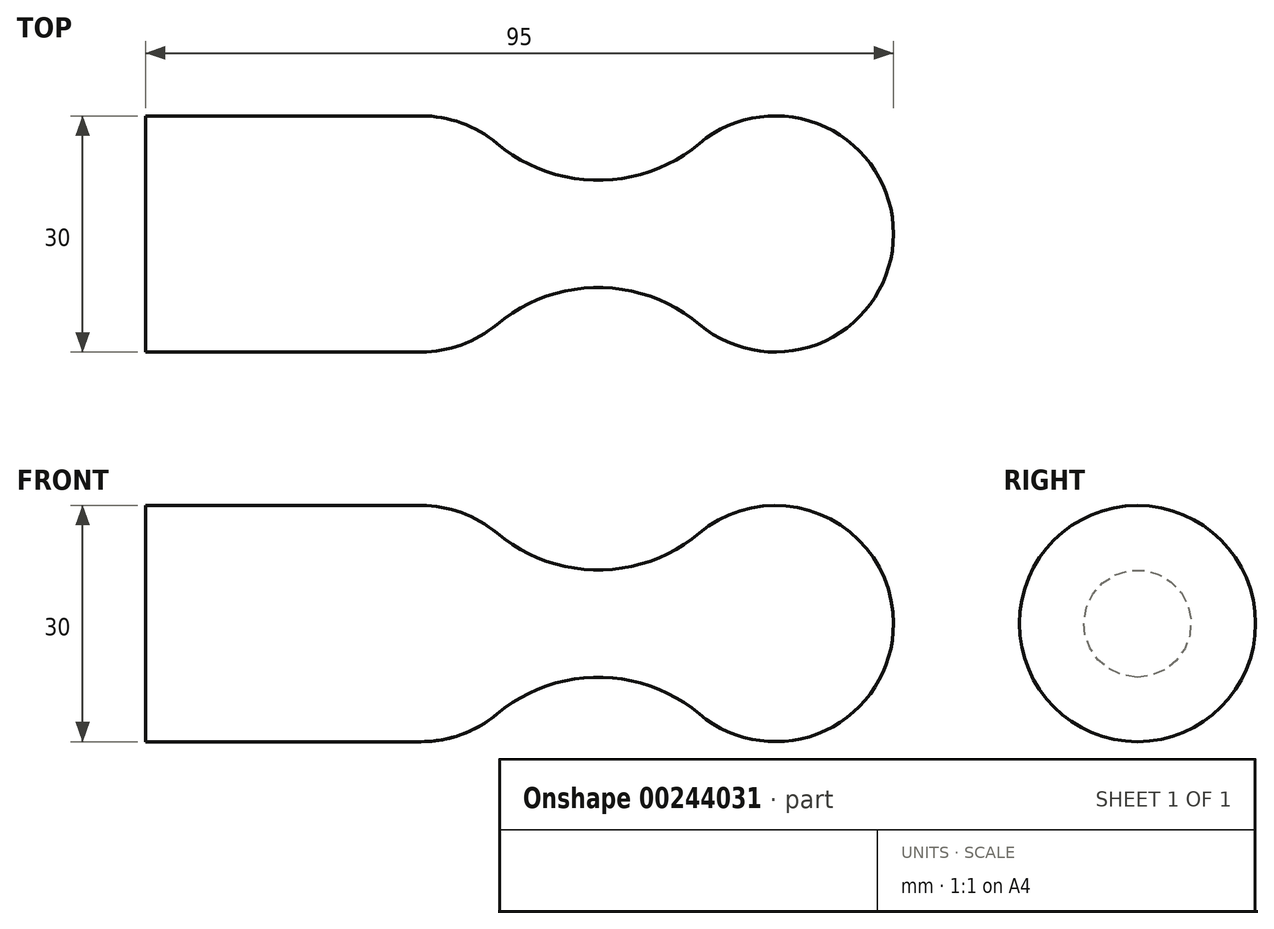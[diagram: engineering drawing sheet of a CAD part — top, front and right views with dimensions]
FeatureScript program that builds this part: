
annotation { "Feature Type Name" : "Feature", "Feature Type Description" : "" }
export const myFeature = defineFeature(function(context is Context, id is Id, definition is map)
    precondition{}
    {
        {
            var Q0;
            Q0=qCreatedBy(makeId("Front.planeOp"),FACE);
            var sketch = newSketch(context, id + "F0", { "sketchPlane" : qUnion([Q0])});
            skArc(sketch, "E0", {"start": v(0, 0) * mm, "mid": v(-8.66, 13.6) * mm, "end": v(-24.64, 11.49) * mm});
            skLineSegment(sketch, "E1", {"start": v(0, 0) * mm, "end": v(-95, 0) * mm});
            skArc(sketch, "E2", {"start": v(-50.36, 11.49) * mm, "mid": v(-54.87, 14.1) * mm, "end": v(-60, 15) * mm});
            skArc(sketch, "E3", {"start": v(-50.36, 11.49) * mm, "mid": v(-37.5, 6.8) * mm, "end": v(-24.64, 11.49) * mm});
            skLineSegment(sketch, "E4", {"start": v(-60, 15) * mm, "end": v(-95, 15) * mm});
            skLineSegment(sketch, "E5", {"start": v(-95, 0) * mm, "end": v(-95, 15) * mm});
            skSolve(sketch);
        }
        {
            var Q0;
            Q0=makeQuery(id+"F0.imprint","IMPRINT",FACE,{"disambiguationData":[TD([[makeQuery(id+"F0.imprint","IMPRINT",EDGE,{"derivedFrom":sQuery(id+"F0.wireOp",EDGE,"E0")}),1.0]])]});
            var Q1;
            Q1=sQuery(id+"F0.wireOp",EDGE,"E1");
            revolve(context, id + "F1", {"entities" : qUnion([Q0]), "axis" : qUnion([Q1]), "revolveType" : RevolveType.FULL});
        }
    });
